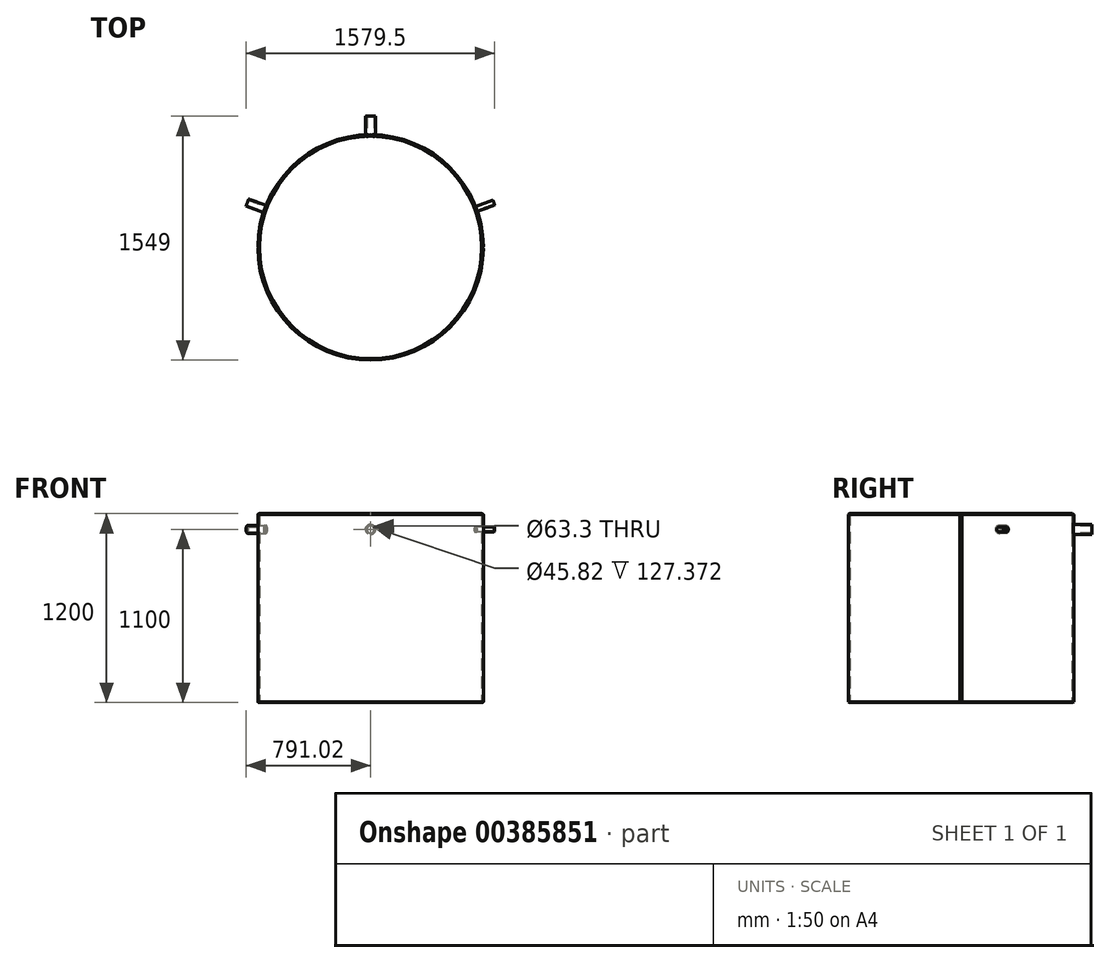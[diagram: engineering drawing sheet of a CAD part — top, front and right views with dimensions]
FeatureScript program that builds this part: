
annotation { "Feature Type Name" : "Feature", "Feature Type Description" : "" }
export const myFeature = defineFeature(function(context is Context, id is Id, definition is map)
    precondition{}
    {
        {
            var Q0;
            Q0=qCreatedBy(makeId("Top.planeOp"),FACE);
            var sketch = newSketch(context, id + "F0", { "sketchPlane" : qUnion([Q0])});
            skArc(sketch, "E0", {"start": v(-5.53, 715.98) * mm, "mid": v(-716, 0) * mm, "end": v(-5.53, -715.98) * mm});
            skArc(sketch, "E1.0", {"start": v(-1.5, 706) * mm, "mid": v(-706, 0) * mm, "end": v(-1.5, -706) * mm});
            skLineSegment(sketch, "E2", {"start": v(0, 716) * mm, "end": v(0, -716) * mm, "construction": true});
            skLineSegment(sketch, "E3", {"start": v(-716, 0) * mm, "end": v(716, 0) * mm, "construction": true});
            skLineSegment(sketch, "E4", {"start": v(1.5, 709) * mm, "end": v(1.5, 706) * mm});
            skCircle(sketch, "E5.0", {"center": v(0, 0) * mm, "radius": 709 * mm, "construction": true});
            skLineSegment(sketch, "E6", {"start": v(1.5, 709) * mm, "end": v(5.53, 715.98) * mm});
            skLineSegment(sketch, "E7.MirrorCS", {"start": v(-1.5, 709) * mm, "end": v(-1.5, 706) * mm});
            skLineSegment(sketch, "E8.MirrorCS", {"start": v(-1.5, 709) * mm, "end": v(-5.53, 715.98) * mm});
            skLineSegment(sketch, "E9.MirrorCS", {"start": v(1.5, -709) * mm, "end": v(1.5, -706) * mm});
            skLineSegment(sketch, "E10.MirrorCS", {"start": v(-1.5, -709) * mm, "end": v(-1.5, -706) * mm});
            skLineSegment(sketch, "E11.MirrorCS", {"start": v(-1.5, -709) * mm, "end": v(-5.53, -715.98) * mm});
            skLineSegment(sketch, "E12.MirrorCS", {"start": v(1.5, -709) * mm, "end": v(5.53, -715.98) * mm});
            skArc(sketch, "E13.trimOffspring", {"start": v(5.53, -715.98) * mm, "mid": v(716, 0) * mm, "end": v(5.53, 715.98) * mm});
            skArc(sketch, "E14.trimOffspring", {"start": v(1.5, -706) * mm, "mid": v(706, 0) * mm, "end": v(1.5, 706) * mm});
            skSolve(sketch);
        }
        {
            var Q0;
            Q0=qSketchRegion(id+"F0",true);
            extrude(context, id + "F1", {"entities" : qUnion([Q0]), "endBound" : BoundingType.SYMMETRIC, "depth" : 1200 * mm});
        }
        {
            var Q0;
            Q0=qCreatedBy(makeId("Right.planeOp"),FACE);
            var sketch = newSketch(context, id + "F2", { "sketchPlane" : qUnion([Q0])});
            skLineSegment(sketch, "E15", {"start": v(0, 612.66) * mm, "end": v(0, -646.3) * mm, "construction": true});
            skLineSegment(sketch, "E16", {"start": v(-709, 600) * mm, "end": v(-726.72, 600) * mm});
            skLineSegment(sketch, "E17", {"start": v(-726.72, 600) * mm, "end": v(-726.72, 589.77) * mm});
            skLineSegment(sketch, "E18", {"start": v(-726.72, 589.77) * mm, "end": v(-709, 600) * mm});
            skLineSegment(sketch, "E19", {"start": v(-747.88, 0) * mm, "end": v(755.94, 0) * mm, "construction": true});
            skLineSegment(sketch, "E20.MirrorCS", {"start": v(-726.72, -600) * mm, "end": v(-726.72, -589.77) * mm});
            skLineSegment(sketch, "E21.MirrorCS", {"start": v(-709, -600) * mm, "end": v(-726.72, -600) * mm});
            skLineSegment(sketch, "E22.MirrorCS", {"start": v(-726.72, -589.77) * mm, "end": v(-709, -600) * mm});
            skSolve(sketch);
        }
        {
            var Q0;
            Q0=qSketchRegion(id+"F2",true);
            var Q1;
            Q1=sQuery(id+"F2.wireOp",EDGE,"E15");
            revolve(context, id + "F3", {"operationType" : NewBodyOperationType.REMOVE, "entities" : qUnion([Q0]), "axis" : qUnion([Q1]), "revolveType" : RevolveType.FULL, "oppositeDirection" : true});
        }
        {
            var Q0;
            Q0=qSketchRegion(id+"F2",true);
            var Q1;
            Q1=sQuery(id+"F2.wireOp",EDGE,"E15");
            revolve(context, id + "F4", {"operationType" : NewBodyOperationType.REMOVE, "entities" : qUnion([Q0]), "axis" : qUnion([Q1]), "revolveType" : RevolveType.FULL, "oppositeDirection" : true});
        }
        {
            var Q0;
            Q0=sQuery(id+"F2.wireOp",EDGE,"E15");
            cPlane(context, id + "F5", {"entities" : qUnion([Q0]), "cplaneType" : CPlaneType.LINE_ANGLE, "offset" : 25 * mm, "angle" : 70 * degree, "oppositeDirection" : true, "width" : 150 * mm, "height" : 150 * mm});
        }
        {
            var Q0;
            Q0=sQuery(id+"F2.wireOp",EDGE,"E15");
            cPlane(context, id + "F6", {"entities" : qUnion([Q0]), "cplaneType" : CPlaneType.LINE_ANGLE, "offset" : 25 * mm, "angle" : 70 * degree, "width" : 150 * mm, "height" : 150 * mm});
        }
        {
            var Q0;
            Q0=qCreatedBy(makeId("Right.planeOp"),FACE);
            var sketch = newSketch(context, id + "F7", { "sketchPlane" : qUnion([Q0])});
            skCircle(sketch, "E23", {"center": v(0, 500) * mm, "radius": 31.65 * mm});
            skCircle(sketch, "E24", {"center": v(0, 500) * mm, "radius": 22.9 * mm});
            skSolve(sketch);
        }
        {
            var Q0;
            Q0=qCreatedBy(id+"F5.planeOp",FACE);
            var sketch = newSketch(context, id + "F8", { "sketchPlane" : qUnion([Q0])});
            skCircle(sketch, "E25", {"center": v(0, 500) * mm, "radius": 17 * mm});
            skCircle(sketch, "E26", {"center": v(0, 500) * mm, "radius": 24.15 * mm});
            skSolve(sketch);
        }
        {
            var Q0;
            Q0=qCreatedBy(id+"F6.planeOp",FACE);
            var sketch = newSketch(context, id + "F9", { "sketchPlane" : qUnion([Q0])});
            skCircle(sketch, "E27", {"center": v(0, 500) * mm, "radius": 10.35 * mm});
            skCircle(sketch, "E28", {"center": v(0, 500) * mm, "radius": 16.7 * mm});
            skSolve(sketch);
        }
        {
            var Q0;
            Q0=makeQuery(id+"F7.imprint","IMPRINT",FACE,{"disambiguationData":[TD([[makeQuery(id+"F7.imprint","IMPRINT",EDGE,{"derivedFrom":sQuery(id+"F7.wireOp",EDGE,"E23")}),1.0]])]});
            var Q1;
            Q1=makeQuery(id+"F7.imprint","IMPRINT",FACE,{"disambiguationData":[TD([[makeQuery(id+"F7.imprint","IMPRINT",EDGE,{"derivedFrom":sQuery(id+"F7.wireOp",EDGE,"E24")}),1.0]])]});
            extrude(context, id + "F10", {"entities" : qUnion([Q0, Q1]), "operationType" : NewBodyOperationType.REMOVE, "endBound" : BoundingType.THROUGH_ALL, "depth" : 25 * mm});
        }
        {
            var Q0;
            Q0=makeQuery(id+"F7.imprint","IMPRINT",FACE,{"disambiguationData":[TD([[makeQuery(id+"F7.imprint","IMPRINT",EDGE,{"derivedFrom":sQuery(id+"F7.wireOp",EDGE,"E23")}),1.0]])]});
            extrude(context, id + "F11", {"entities" : qUnion([Q0]), "depth" : 833 * mm});
        }
        {
            var Q0;
            Q0=makeQuery(id+"F8.imprint","IMPRINT",FACE,{"disambiguationData":[TD([[makeQuery(id+"F8.imprint","IMPRINT",EDGE,{"derivedFrom":sQuery(id+"F8.wireOp",EDGE,"E25")}),1.0]])]});
            var Q1;
            Q1=makeQuery(id+"F8.imprint","IMPRINT",FACE,{"disambiguationData":[TD([[makeQuery(id+"F8.imprint","IMPRINT",EDGE,{"derivedFrom":sQuery(id+"F8.wireOp",EDGE,"E25")}),-1.0]])]});
            extrude(context, id + "F12", {"entities" : qUnion([Q0, Q1]), "operationType" : NewBodyOperationType.REMOVE, "endBound" : BoundingType.THROUGH_ALL, "oppositeDirection" : true, "depth" : 25 * mm});
        }
        {
            var Q0;
            Q0=makeQuery(id+"F8.imprint","IMPRINT",FACE,{"disambiguationData":[TD([[makeQuery(id+"F8.imprint","IMPRINT",EDGE,{"derivedFrom":sQuery(id+"F8.wireOp",EDGE,"E25")}),-1.0]])]});
            extrude(context, id + "F13", {"entities" : qUnion([Q0]), "oppositeDirection" : true, "depth" : 833 * mm});
        }
        {
            var Q0;
            Q0=makeQuery(id+"F9.imprint","IMPRINT",FACE,{"disambiguationData":[TD([[makeQuery(id+"F9.imprint","IMPRINT",EDGE,{"derivedFrom":sQuery(id+"F9.wireOp",EDGE,"E27")}),1.0]])]});
            var Q1;
            Q1=makeQuery(id+"F9.imprint","IMPRINT",FACE,{"disambiguationData":[TD([[makeQuery(id+"F9.imprint","IMPRINT",EDGE,{"derivedFrom":sQuery(id+"F9.wireOp",EDGE,"E27")}),-1.0]])]});
            extrude(context, id + "F14", {"entities" : qUnion([Q0, Q1]), "operationType" : NewBodyOperationType.REMOVE, "endBound" : BoundingType.THROUGH_ALL, "oppositeDirection" : true, "depth" : 25 * mm});
        }
        {
            var Q0;
            Q0=makeQuery(id+"F9.imprint","IMPRINT",FACE,{"disambiguationData":[TD([[makeQuery(id+"F9.imprint","IMPRINT",EDGE,{"derivedFrom":sQuery(id+"F9.wireOp",EDGE,"E27")}),-1.0]])]});
            extrude(context, id + "F15", {"entities" : qUnion([Q0]), "oppositeDirection" : true, "depth" : 833 * mm});
        }
        {
            var Q0;
            Q0=qCreatedBy(makeId("Top.planeOp"),FACE);
            var sketch = newSketch(context, id + "F16", { "sketchPlane" : qUnion([Q0])});
            skCircle(sketch, "E29", {"center": v(0, 0) * mm, "radius": 706 * mm});
            skSolve(sketch);
        }
        {
            var Q0;
            Q0 = qSketchRegion(id + "F16", true);
            extrude(context, id + "F17", {"entities" : qUnion([Q0]), "operationType" : NewBodyOperationType.REMOVE, "endBound" : BoundingType.THROUGH_ALL, "depth" : 25 * mm});
        }
        {
            var Q0;
            Q0 = qSketchRegion(id + "F16", true);
            extrude(context, id + "F18", {"entities" : qUnion([Q0]), "operationType" : NewBodyOperationType.REMOVE, "endBound" : BoundingType.THROUGH_ALL, "depth" : 25 * mm});
        }
        {
            var Q0;
            Q0 = qSketchRegion(id + "F16", true);
            extrude(context, id + "F19", {"entities" : qUnion([Q0]), "operationType" : NewBodyOperationType.REMOVE, "endBound" : BoundingType.THROUGH_ALL, "depth" : 25 * mm});
        }
        {
            var Q0;
            Q0=makeQuery(id+"F1.opExtrude","SWEPT_BODY",BODY,{"disambiguationData":[OSD([sQuery(id+"F0.wireOp",EDGE,"E0"),sQuery(id+"F0.wireOp",EDGE,"E1.0"),sQuery(id+"F0.wireOp",EDGE,"E7.MirrorCS"),sQuery(id+"F0.wireOp",EDGE,"E8.MirrorCS"),sQuery(id+"F0.wireOp",EDGE,"E10.MirrorCS"),sQuery(id+"F0.wireOp",EDGE,"E11.MirrorCS")])]});
            var Q1;
            Q1=makeQuery(id+"F1.opExtrude","SWEPT_BODY",BODY,{"disambiguationData":[OSD([sQuery(id+"F0.wireOp",EDGE,"E4"),sQuery(id+"F0.wireOp",EDGE,"E6"),sQuery(id+"F0.wireOp",EDGE,"E9.MirrorCS"),sQuery(id+"F0.wireOp",EDGE,"E12.MirrorCS"),sQuery(id+"F0.wireOp",EDGE,"E13.trimOffspring"),sQuery(id+"F0.wireOp",EDGE,"E14.trimOffspring")])]});
            var Q2;
            Q2=makeQuery(id+"F11.opExtrude","SWEPT_BODY",BODY,{"disambiguationData":[OSD([sQuery(id+"F7.wireOp",EDGE,"E23"),sQuery(id+"F7.wireOp",EDGE,"E24")])]});
            var Q3;
            Q3=makeQuery(id+"F13.opExtrude","SWEPT_BODY",BODY,{"disambiguationData":[OSD([sQuery(id+"F8.wireOp",EDGE,"E25"),sQuery(id+"F8.wireOp",EDGE,"E26")])]});
            var Q4;
            Q4=makeQuery(id+"F15.opExtrude","SWEPT_BODY",BODY,{"disambiguationData":[OSD([sQuery(id+"F9.wireOp",EDGE,"E27"),sQuery(id+"F9.wireOp",EDGE,"E28")])]});
            var Q5;
            Q5=sQuery(id+"F2.wireOp",EDGE,"E15");
            transform(context, id + "F20", {"entities" : qUnion([Q0, Q1, Q2, Q3, Q4]), "transformType" : TransformType.ROTATION, "transformAxis" : qUnion([Q5]), "angle" : 90 * degree, "oppositeDirection" : true, "makeCopy" : false});
        }
    });
